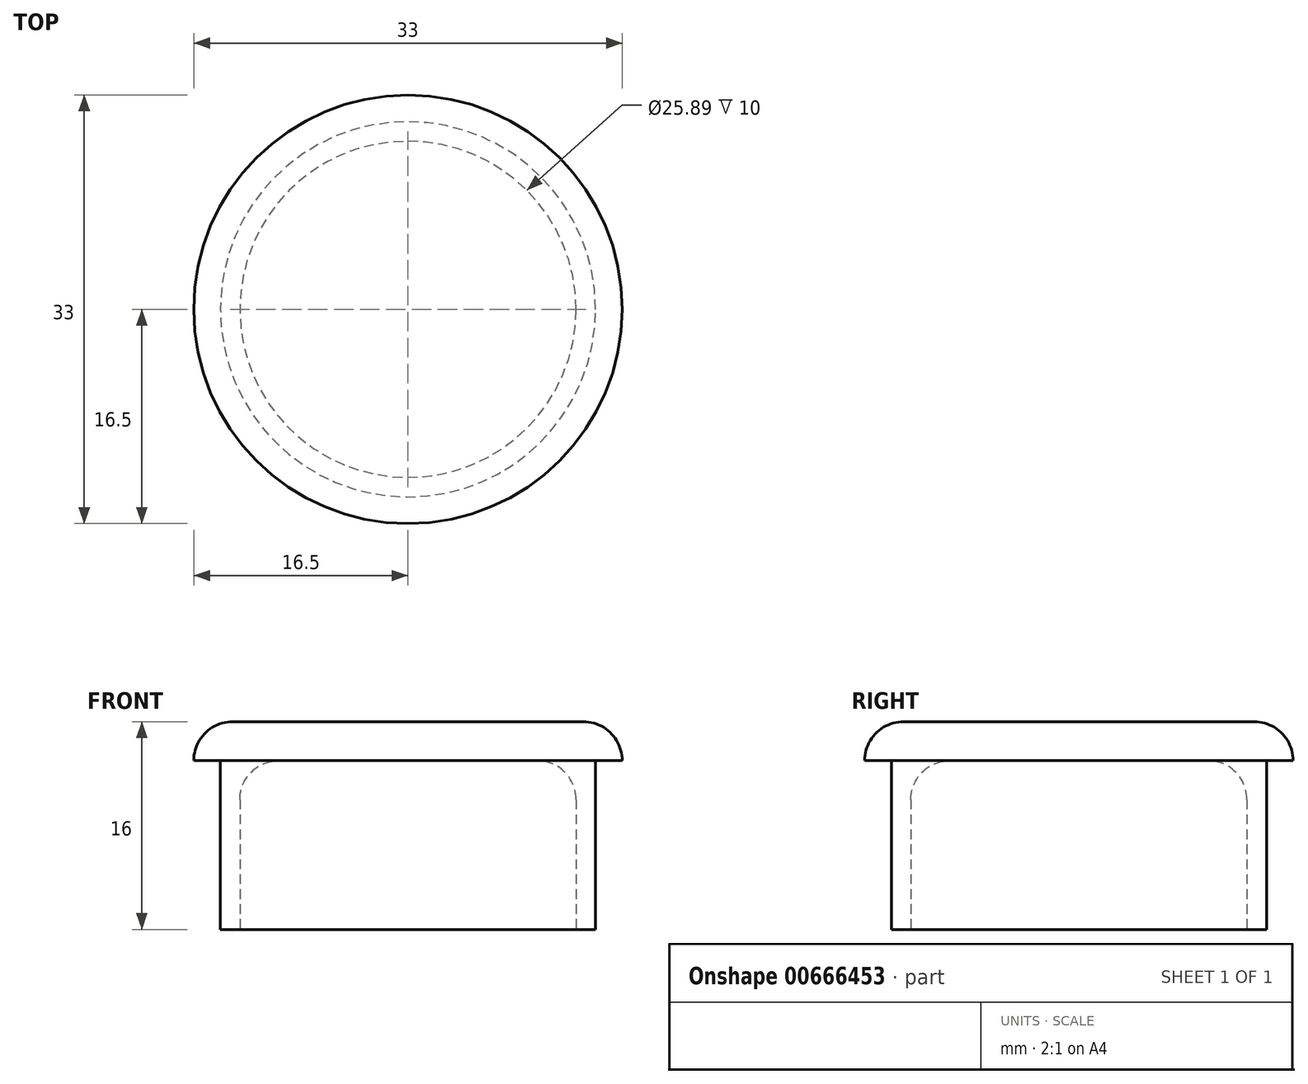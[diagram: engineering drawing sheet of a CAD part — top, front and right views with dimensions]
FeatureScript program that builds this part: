
annotation { "Feature Type Name" : "Feature", "Feature Type Description" : "" }
export const myFeature = defineFeature(function(context is Context, id is Id, definition is map)
    precondition{}
    {
        {
            var Q0;
            Q0=qCreatedBy(makeId("Top.planeOp"),FACE);
            var sketch = newSketch(context, id + "F0", { "sketchPlane" : qUnion([Q0])});
            skCircle(sketch, "E0", {"center": v(0, 0) * mm, "radius": 14.45 * mm});
            skCircle(sketch, "E1", {"center": v(0, 0) * mm, "radius": 12.95 * mm});
            skSolve(sketch);
        }
        {
            var Q0;
            Q0 = qSketchRegion(id + "F0", true);
            extrude(context, id + "F1", {"entities" : qUnion([Q0]), "depth" : 13 * mm, "offsetDistance" : 25 * mm});
        }
        {
            var Q0;
            Q0=makeQuery(id+"F1.opExtrude","CAP_FACE",FACE,{"disambiguationData":[OSD([sQuery(id+"F0.wireOp",EDGE,"E0"),sQuery(id+"F0.wireOp",EDGE,"E1")])],"isStart":false});
            var sketch = newSketch(context, id + "F2", { "sketchPlane" : qUnion([Q0])});
            skCircle(sketch, "E2", {"center": v(0, 0) * mm, "radius": 16.5 * mm});
            skSolve(sketch);
        }
        {
            var Q0;
            Q0 = qSketchRegion(id + "F2", true);
            extrude(context, id + "F3", {"entities" : qUnion([Q0]), "operationType" : NewBodyOperationType.ADD, "depth" : 3 * mm, "offsetDistance" : 25 * mm});
        }
        {
            var Q0;
            Q0=makeQuery(id+"F3.opExtrude","CAP_EDGE",EDGE,{"disambiguationData":[OSD([sQuery(id+"F2.wireOp",EDGE,"E2")])],"isStart":false});
            var Q1;
            Q1=makeQuery(id+"F1.opExtrude","CAP_EDGE",EDGE,{"disambiguationData":[OSD([sQuery(id+"F0.wireOp",EDGE,"E1")])],"isStart":false});
            fillet(context, id + "F4", {"entities" : qUnion([Q0, Q1]), "radius" : 3 * mm, "tangentPropagation" : true, "allowEdgeOverflow" : false});
        }
    });
